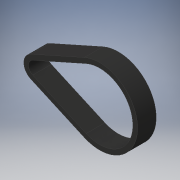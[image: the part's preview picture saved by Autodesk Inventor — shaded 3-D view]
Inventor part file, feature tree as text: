
AUTODESK INVENTOR PART (.ipt)
format: ipt  version: 2019.4 (Build 234330000, 330)  size: 122,368 bytes
history: native  units: mm
features: extrude x1, sketch x1
ambient origin geometry x8: Origin, YZ Plane, XZ Plane, XY Plane, X Axis, Y Axis, Z Axis, Center Point
bodies: Solid1 (feature_tree)
feature tree (2):
  extrude  "Extrusion1"  Depth=51.5mm
  sketch  "Sketch1"  dims[d0=14.52mm d1=51.5mm d4=56.53mm d8=15.0mm d9=0.0mm d10=3.81mm d12=3.81mm d13=1.601mm d14=1.631mm]
